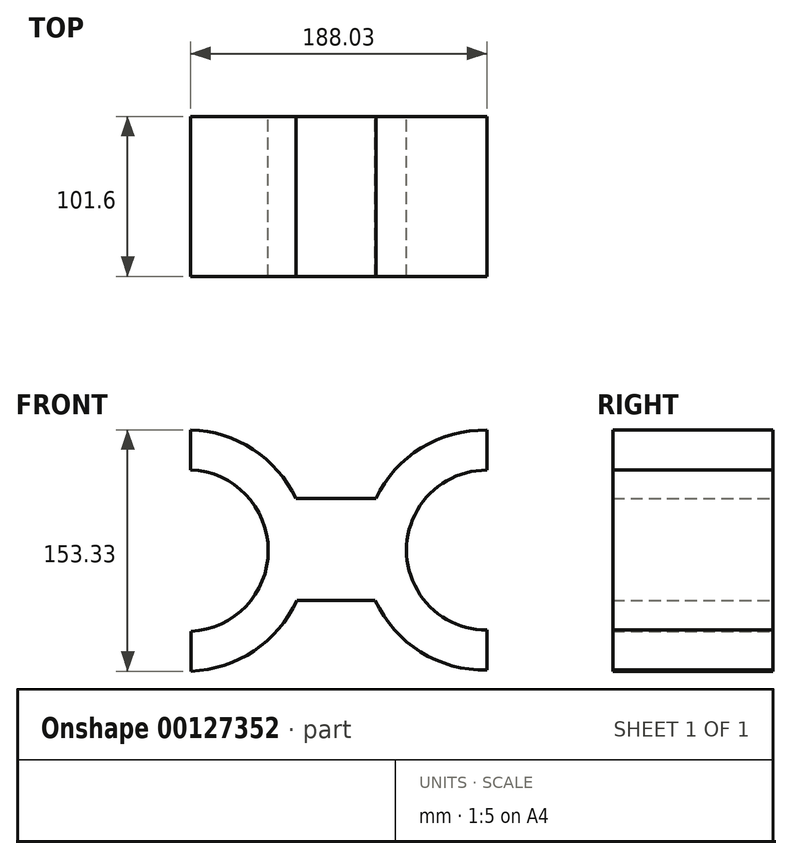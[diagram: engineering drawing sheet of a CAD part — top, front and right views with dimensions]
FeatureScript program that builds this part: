
annotation { "Feature Type Name" : "Feature", "Feature Type Description" : "" }
export const myFeature = defineFeature(function(context is Context, id is Id, definition is map)
    precondition{}
    {
        {
            var Q0;
            Q0=qCreatedBy(makeId("Front.planeOp"),FACE);
            var sketch = newSketch(context, id + "F0", { "sketchPlane" : qUnion([Q0])});
            skLineSegment(sketch, "E0", {"start": v(76.26, 74.28) * mm, "end": v(76.26, 99.68) * mm});
            skLineSegment(sketch, "E1", {"start": v(76.26, -27.32) * mm, "end": v(76.26, -52.72) * mm});
            skArc(sketch, "E2", {"start": v(76.26, 74.28) * mm, "mid": v(25.31, 23.48) * mm, "end": v(76.26, -27.32) * mm});
            skArc(sketch, "E3", {"start": v(76.26, 99.68) * mm, "mid": v(34.64, 88.37) * mm, "end": v(5.82, 56.29) * mm});
            skLineSegment(sketch, "E4", {"start": v(5.42, -8.47) * mm, "end": v(-44.37, -8.47) * mm});
            skLineSegment(sketch, "E5", {"start": v(-44.98, 56.29) * mm, "end": v(5.82, 56.29) * mm});
            skArc(sketch, "E6", {"start": v(-111.6, -53.4) * mm, "mid": v(-71.58, -40.52) * mm, "end": v(-44.37, -8.47) * mm});
            skLineSegment(sketch, "E7", {"start": v(-111.77, 99.92) * mm, "end": v(-111.77, 74.52) * mm});
            skLineSegment(sketch, "E8", {"start": v(-111.6, -53.4) * mm, "end": v(-111.6, -28) * mm});
            skArc(sketch, "E9", {"start": v(-111.6, -28) * mm, "mid": v(-62.57, 23.34) * mm, "end": v(-111.77, 74.52) * mm});
            skArc(sketch, "E10.trimOffspring", {"start": v(5.42, -8.47) * mm, "mid": v(34.24, -41.16) * mm, "end": v(76.26, -52.72) * mm});
            skArc(sketch, "E11.trimOffspring", {"start": v(-44.98, 56.29) * mm, "mid": v(-72.26, 87.47) * mm, "end": v(-111.77, 99.92) * mm});
            skSolve(sketch);
        }
        {
            var Q0;
            Q0 = qSketchRegion(id + "F0", true);
            extrude(context, id + "F1", {"entities" : qUnion([Q0]), "depth" : 101.6 * mm});
        }
    });
